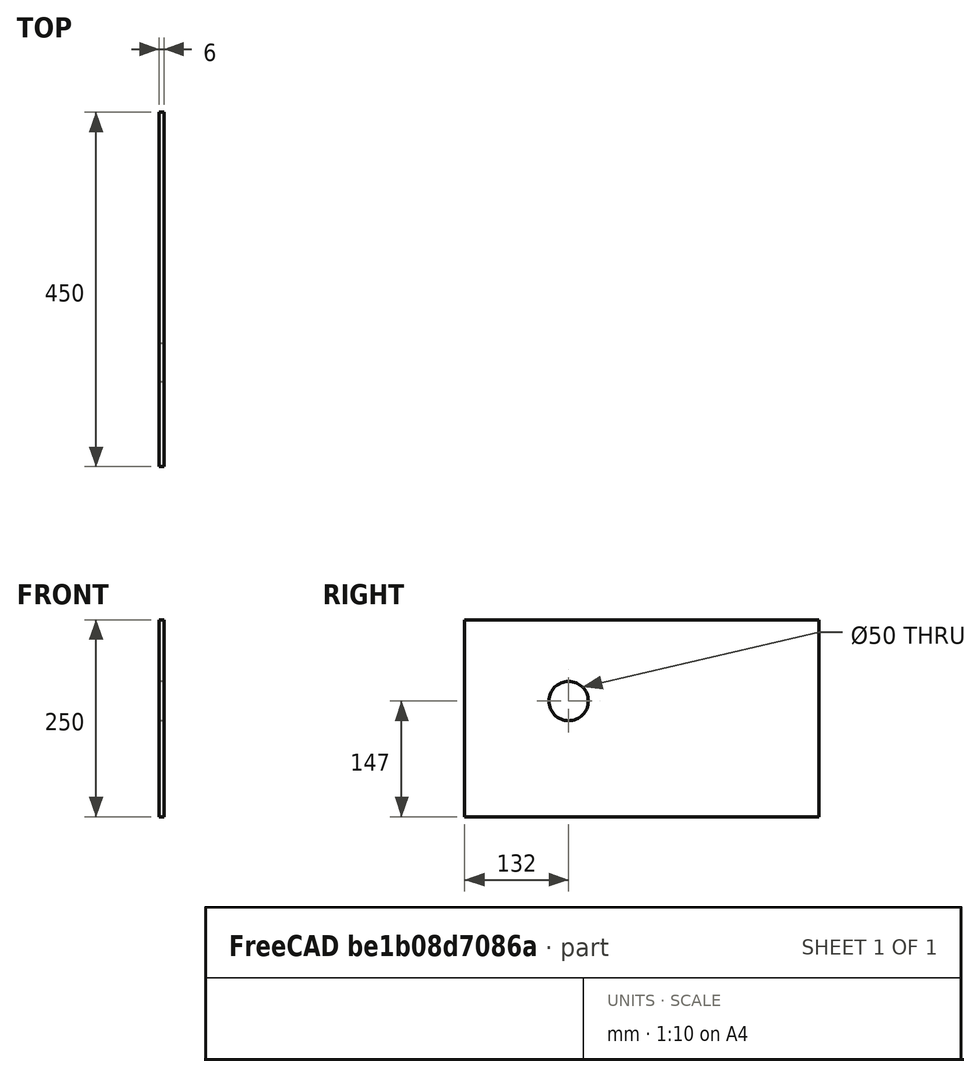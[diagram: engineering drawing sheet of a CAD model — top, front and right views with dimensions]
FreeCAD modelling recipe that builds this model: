
FCSTD DOCUMENT  (FreeCAD 0.18R4 (GitTag))
Label: Gabinete_Lateral1
License: All rights reserved
LicenseURL: http://en.wikipedia.org/wiki/All_rights_reserved
objects: Sketcher::SketchObject×1, PartDesign::Pad×1, PartDesign::Body×1
note: 4 computed .brp shape members not serialized (recipe doc carries the construction recipe); baked Part::Feature solids carry a one-line shape summary decoded from their .brp

FEATURE [Sketcher::SketchObject] Sketch
  MapMode = 5
  Placement = pos=(0,0,0) rot=(0.57735,0.57735,0.57735;2.0944rad)
  Support = -> [YZ_Plane]
  sketch-geometry (5):
    g0: LineSegment StartX=0 StartY=0 StartZ=0 EndX=450 EndY=0 EndZ=0
    g1: LineSegment StartX=450 StartY=0 StartZ=0 EndX=450 EndY=250 EndZ=0
    g2: LineSegment StartX=450 StartY=250 StartZ=0 EndX=0 EndY=250 EndZ=0
    g3: LineSegment StartX=0 StartY=250 StartZ=0 EndX=0 EndY=0 EndZ=0
    g4: Circle CenterX=132 CenterY=147 CenterZ=0 NormalX=0 NormalY=0 NormalZ=1 AngleXU=0 Radius=25
  constraints (14):
    c: Coincident(g0,g1)
    c: Coincident(g1,g2)
    c: Coincident(g2,g3)
    c: Coincident(g3,g0)
    c: Horizontal(g0)
    c: Horizontal(g2)
    c: Vertical(g1)
    c: Vertical(g3)
    c: Coincident(g0,g-1)
    c: DistanceX(g0,g0) = 450
    c: DistanceY(g3,g3) = 250
    c: Radius(g4) = 25
    c: Distance(g4,g0) = 147
    c: Distance(g4,g3) = 132
FEATURE [PartDesign::Pad] Pad
  Length = 6
  Length2 = 100
  Placement = pos=(0,0,0) rot=(0.57735,0.57735,0.57735;2.0944rad)
  Profile = -> Sketch
  Type = 0
FEATURE [PartDesign::Body] Body
  Group = -> [Sketch,Pad]
  Origin = -> Origin
  Tip = -> Pad
